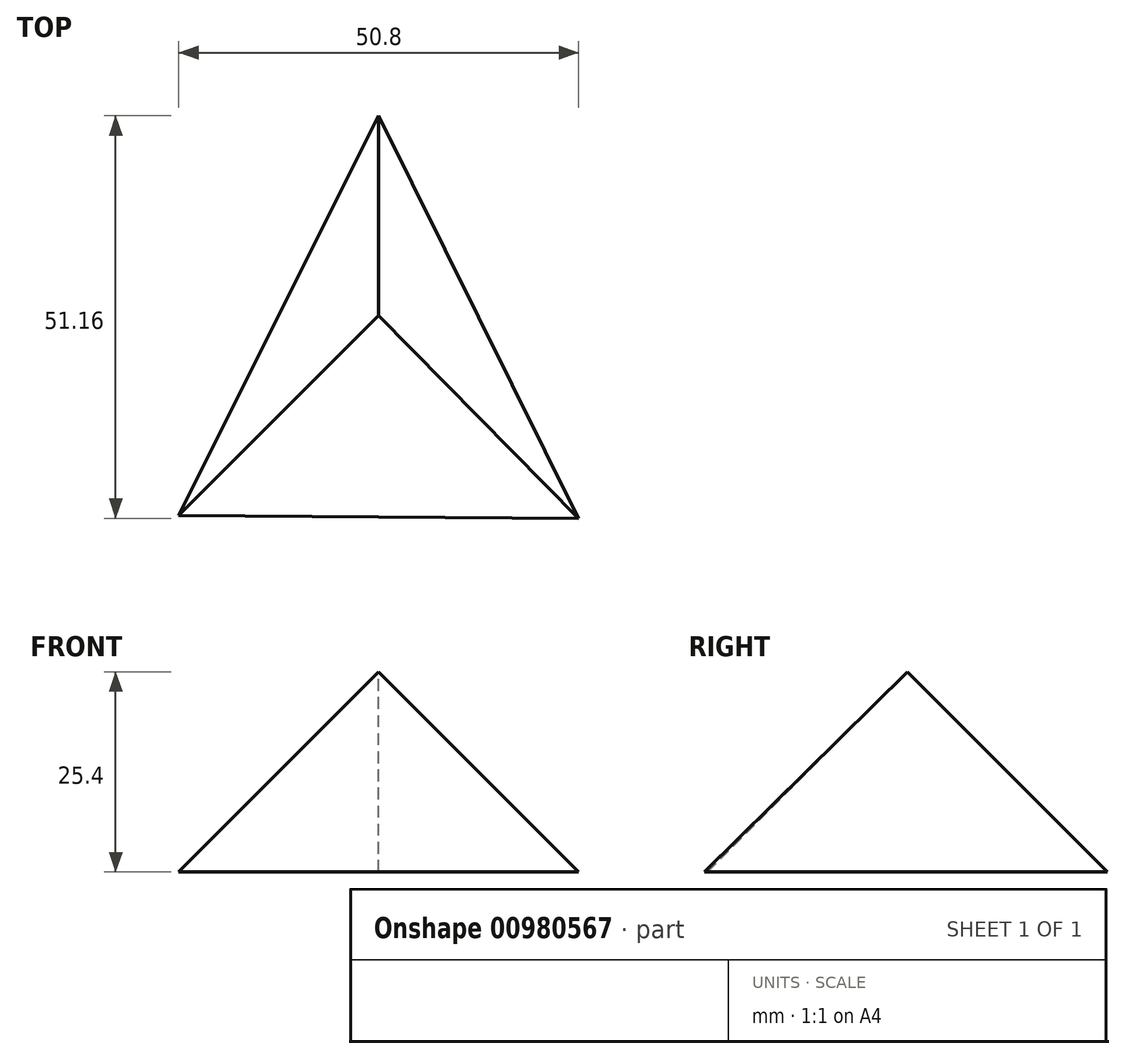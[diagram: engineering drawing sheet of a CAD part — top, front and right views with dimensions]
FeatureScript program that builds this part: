
annotation { "Feature Type Name" : "Feature", "Feature Type Description" : "" }
export const myFeature = defineFeature(function(context is Context, id is Id, definition is map)
    precondition{}
    {
        {
            var Q0;
            Q0=qCreatedBy(makeId("Top.planeOp"),FACE);
            var sketch = newSketch(context, id + "F0", { "sketchPlane" : qUnion([Q0])});
            skLineSegment(sketch, "E0", {"start": v(-25.4, -25.4) * mm, "end": v(0, 25.4) * mm});
            skLineSegment(sketch, "E1", {"start": v(0, 25.4) * mm, "end": v(25.4, -25.76) * mm});
            skLineSegment(sketch, "E2", {"start": v(25.4, -25.76) * mm, "end": v(-25.4, -25.4) * mm});
            skSolve(sketch);
        }
        {
            var Q0;
            Q0=qCreatedBy(makeId("Front.planeOp"),FACE);
            var sketch = newSketch(context, id + "F1", { "sketchPlane" : qUnion([Q0])});
            skPoint(sketch, "E3", {"position": v(0, 25.4) * mm});
            skPoint(sketch, "E4", {"position": v(0.15, 25.1) * mm});
            skSolve(sketch);
        }
        {
            var Q0;
            Q0=makeQuery(id+"F0.imprint","IMPRINT",FACE,{"disambiguationData":[TD([[makeQuery(id+"F0.imprint","IMPRINT",EDGE,{"derivedFrom":sQuery(id+"F0.wireOp",EDGE,"E0")}),-1.0]])]});
            var Q1;
            Q1=sQuery(id+"F1.wireOp",VERTEX,"E3");
            loft(context, id + "F2", {"sheetProfilesArray" : [{ "sheetProfileEntities" : qUnion([Q0]) }, { "sheetProfileEntities" : qUnion([Q1]) }]});
        }
    });
